# Revit family: Flexit UNI 4 R E EC L 230
name_source: partatom
category: Mechanical Equipment
revit_build: Autodesk Revit 2015 (Build: 20140322_1515(x64)
units: mm (PartAtom-declared; Revit-internal decimal feet)

## types (1)
- Flexit UNI 4 R E EC L 230
    Dimensions = 900 537 700 mm
    Exhaust Dimensions = 160 mm
    Exhaust Frequency band = 63 125 250 500 1k 2k 4k 8k
    Exhaust Sound generation = 68 67 68 63 57 53 42 28 dB
    Exhaust Sound generation, total = 64 dB(A)
    Extract 1 Dimensions = 160 mm
    Extract 1 Frequency band = 63 125 250 500 1k 2k 4k 8k
    Extract 1 Sound generation = 59 57 56 55 43 30 19 4 dB
    Extract 1 Sound generation, total = 54 dB(A)
    Extract 2 Dimensions = 160 mm
    Extract 2 Frequency band = 63 125 250 500 1k 2k 4k 8k
    Extract 2 Sound generation = 59 57 56 55 43 30 19 4 dB
    Extract 2 Sound generation, total = 54 dB(A)
    Extract 3 Dimensions = 125 mm
    Extract 3 Frequency band = 63 125 250 500 1k 2k 4k 8k
    Extract 3 Sound generation = 59 57 56 55 43 30 19 4 dB
    Extract 3 Sound generation, total = 54 dB(A)
    Extract air flow = 27.8 L/s
    Flexit project file name = K2VE.FLX
    Frequency band = 63 125 250 500 1k 2k 4k 8k
    Outdoor 1 Dimensions = 160 mm
    Outdoor 1 Frequency band = 63 125 250 500 1k 2k 4k 8k
    Outdoor 1 Sound generation = 59 57 56 55 43 30 19 4 dB
    Outdoor 1 Sound generation, total = 54 dB(A)
    Outdoor 2 Dimensions = 160 mm
    Outdoor 2 Frequency band = 63 125 250 500 1k 2k 4k 8k
    Outdoor 2 Sound generation = 59 57 56 55 43 30 19 4 dB
    Outdoor 2 Sound generation, total = 54 dB(A)
    Pressure drop  Extract and Exhaust air ductwork = 100.0 Pa
    Pressure drop  Supply and Outdoor air ductwork = 100.0 Pa
    Sound ambient, total = 31 dB(A)
    Sound data, ambient = 15 26 38 27 22 19 11 2 dB
    Supply Dimensions = 160 mm
    Supply Frequency band = 63 125 250 500 1k 2k 4k 8k
    Supply Sound generation = 68 67 68 63 57 53 42 28 dB
    Supply Sound generation, total = 64 dB(A)
    Supply air flow = 27.8 L/s
    Unit description = Flexit UNI 4 R E EC L 230
    Unit size Extract = 4
    Unit size Supply = 4
    Weight = 86.0 kg
    magiFamilyGeom = MagiCAD_Flexit UNI 4 R E EC L 230
    magiFlags = 0
    magiPartTypeId = 210
    magiProductId = Flexit UNI 4 R E EC L 230
    magiXML = <Flexit>
  <RevitBlockID>Block1</RevitBlockID>
  <Block id="Block1" view="256" unit_height="700" subtype="1001">
    <prop id="QPDClass">AFA</prop>
    <prop id="ProductKey">Flexit-UNI-4-R-E-EC-L-230</prop>
    <prop id="ProductCode">Flexit UNI 4 R E EC L 230</prop>
    <prop id="UnitName"></prop>
    <prop id="Description" info="Unit description">Flexit UNI 4 R E EC L 230</prop>
    <prop id="ProjectFile" info="Flexit project file name">K2VE.FLX</prop>
    <prop id="Weight" info="Weight" units="kg">86.0</prop>
    <prop id="Dimensions" info="Dimensions" units="mm">900 537 700</prop>
    <prop id="SupplyAirFlow" info="Supply air flow" units="m3/h">100.000</prop>
    <prop id="ExtractAirFlow" info="Extract air flow" units="m3/h">100.000</prop>
    <prop id="SupplyPressureDrop" info="Pressure drop: Supply and Outdoor air ductwork" units="Pa">100</prop>
    <prop id="ExtractPressureDrop" info="Pressure drop: Extract and Exhaust air ductwork" units="Pa">100</prop>
    <prop id="SupplySize" info="Unit size Supply">4</prop>
    <prop id="ExtractSize" info="Unit size Extract">4</prop>
    <prop id="SoundTitle" info="Sound data, ambient"></prop>
    <prop id="SoundTitleOctave" info="Frequency band">63 125 250 500 1k 2k 4k 8k</prop>
    <prop id="SoundAmbient" info="Sound data, ambient" units="dB">15 26 38 27 22 19 11 2</prop>
    <prop id="SoundAmbientTotal" info="Sound ambient, total" units="dB(A)">31</prop>
    <Connection id="Connection1" type="duct" system="outdoor" info="Duct connection outdoor">
      <prop id="Dimension" info="Dimensions" units="mm">160 0 30</prop>
      <prop id="Position">-329 127.500000 365</prop>
      <prop id="Direction">0 0 1</prop>
      <prop id="Normal">-1 0 0</prop>
      <prop id="SoundTitle" info="Sound data"></prop>
      <prop id="SoundTitleOctave" info="Frequency band">63 125 250 500 1k 2k 4k 8k</prop>
      <prop id="SoundGeneration" info="Sound generation" units="dB">59 57 56 55 43 30 19 4</prop>
      <prop id="SoundGenerationTotal" info="Sound generation, total" units="dB(A)">54</prop>
    </Connection>
    <Connection id="Connection2" type="duct" system="supply" info="Duct connection supply">
      <prop id="Dimension" info="Dimensions" units="mm">160 0 30</prop>
      <prop id="Position">329 127.500000 365</prop>
      <prop id="Direction">0 0 1</prop>
      <prop id="Normal">-1 0 0</prop>
      <prop id="SoundTitle" info="Sound data"></prop>
      <prop id="SoundTitleOctave" info="Frequency band">63 125 250 500 1k 2k 4k 8k</prop>
      <prop id="SoundGeneration" info="Sound generation" units="dB">68 67 68 63 57 53 42 28</prop>
      <prop id="SoundGenerationTotal" info="Sound generation, total" units="dB(A)">64</prop>
    </Connection>
    <Connection id="Connection3" type="duct" system="extract" info="Duct connection extract">
      <prop id="Dimension" info="Dimensions" units="mm">160 0 30</prop>
      <prop id="Position">329 -113 365</prop>
      <prop id="Direction">0 0 1</prop>
      <prop id="Normal">-1 0 0</prop>
      <prop id="SoundTitle" info="Sound data"></prop>
      <prop id="SoundTitleOctave" info="Frequency band">63 125 250 500 1k 2k 4k 8k</prop>
      <prop id="SoundGeneration" info="Sound generation" units="dB">59 57 56 55 43 30 19 4</prop>
      <prop id="SoundGenerationTotal" info="Sound generation, total" units="dB(A)">54</prop>
    </Connection>
    <Connection id="Connection4" type="duct" system="exhaust" info="Duct connection exhaust">
      <prop id="Dimension" info="Dimensions" units="mm">160 0 30</prop>
      <prop id="Position">-329 -113 365</prop>
      <prop id="Direction">0 0 1</prop>
      <prop id="Normal">-1 0 0</prop>
      <prop id="SoundTitle" info="Sound data"></prop>
      <prop id="SoundTitleOctave" info="Frequency band">63 125 250 500 1k 2k 4k 8k</prop>
      <prop id="SoundGeneration" info="Sound generation" units="dB">68 67 68 63 57 53 42 28</prop>
      <prop id="SoundGenerationTotal" info="Sound generation, total" units="dB(A)">64</prop>
    </Connection>
    <Connection id="Connection5" type="duct" system="outdoor" info="Duct connection outdoor">
      <prop id="Dimension" info="Dimensions" units="mm">160 0 30</prop>
      <prop id="Position">-332 107.500000 -365</prop>
      <prop id="Direction">0 0 -1</prop>
      <prop id="Normal">1 0 0</prop>
      <prop id="SoundTitle" info="Sound data"></prop>
      <prop id="SoundTitleOctave" info="Frequency band">63 125 250 500 1k 2k 4k 8k</prop>
      <prop id="SoundGeneration" info="Sound generation" units="dB">59 57 56 55 43 30 19 4</prop>
      <prop id="SoundGenerationTotal" info="Sound generation, total" units="dB(A)">54</prop>
    </Connection>
    <Connection id="Connection6" type="duct" system="extract" info="Duct connection extract">
      <prop id="Dimension" info="Dimensions" units="mm">160 0 30</prop>
      <prop id="Position">332 -118 -365</prop>
      <prop id="Direction">0 0 -1</prop>
      <prop id="Normal">1 0 0</prop>
      <prop id="SoundTitle" info="Sound data"></prop>
      <prop id="SoundTitleOctave" info="Frequency band">63 125 250 500 1k 2k 4k 8k</prop>
      <prop id="SoundGeneration" info="Sound generation" units="dB">59 57 56 55 43 30 19 4</prop>
      <prop id="SoundGenerationTotal" info="Sound generation, total" units="dB(A)">54</prop>
    </Connection>
    <Connection id="Connection7" type="duct" system="extract" info="Duct connection extract" kitchen_hood_connection="1">
      <prop id="Dimension" info="Dimensions" units="mm">125 0 30</prop>
      <prop id="Position">0 57.500000 365</prop>
      <prop id="Direction">0 0 1</prop>
      <prop id="Normal">-1 0 0</prop>
      <prop id="SoundTitle" info="Sound data"></prop>
      <prop id="SoundTitleOctave" info="Frequency band">63 125 250 500 1k 2k 4k 8k</prop>
      <prop id="SoundGeneration" info="Sound generation" units="dB">59 57 56 55 43 30 19 4</prop>
      <prop id="SoundGenerationTotal" info="Sound generation, total" units="dB(A)">54</prop>
    </Connection>
    <gm_model <blob elided: 29072 chars, md5=7c449e0d>
  </Block>
  <Blocks />
</Flexit>

## geometry (parser evidence)
native form markers: Sweep x12
no freeform markers — native parametric forms only
